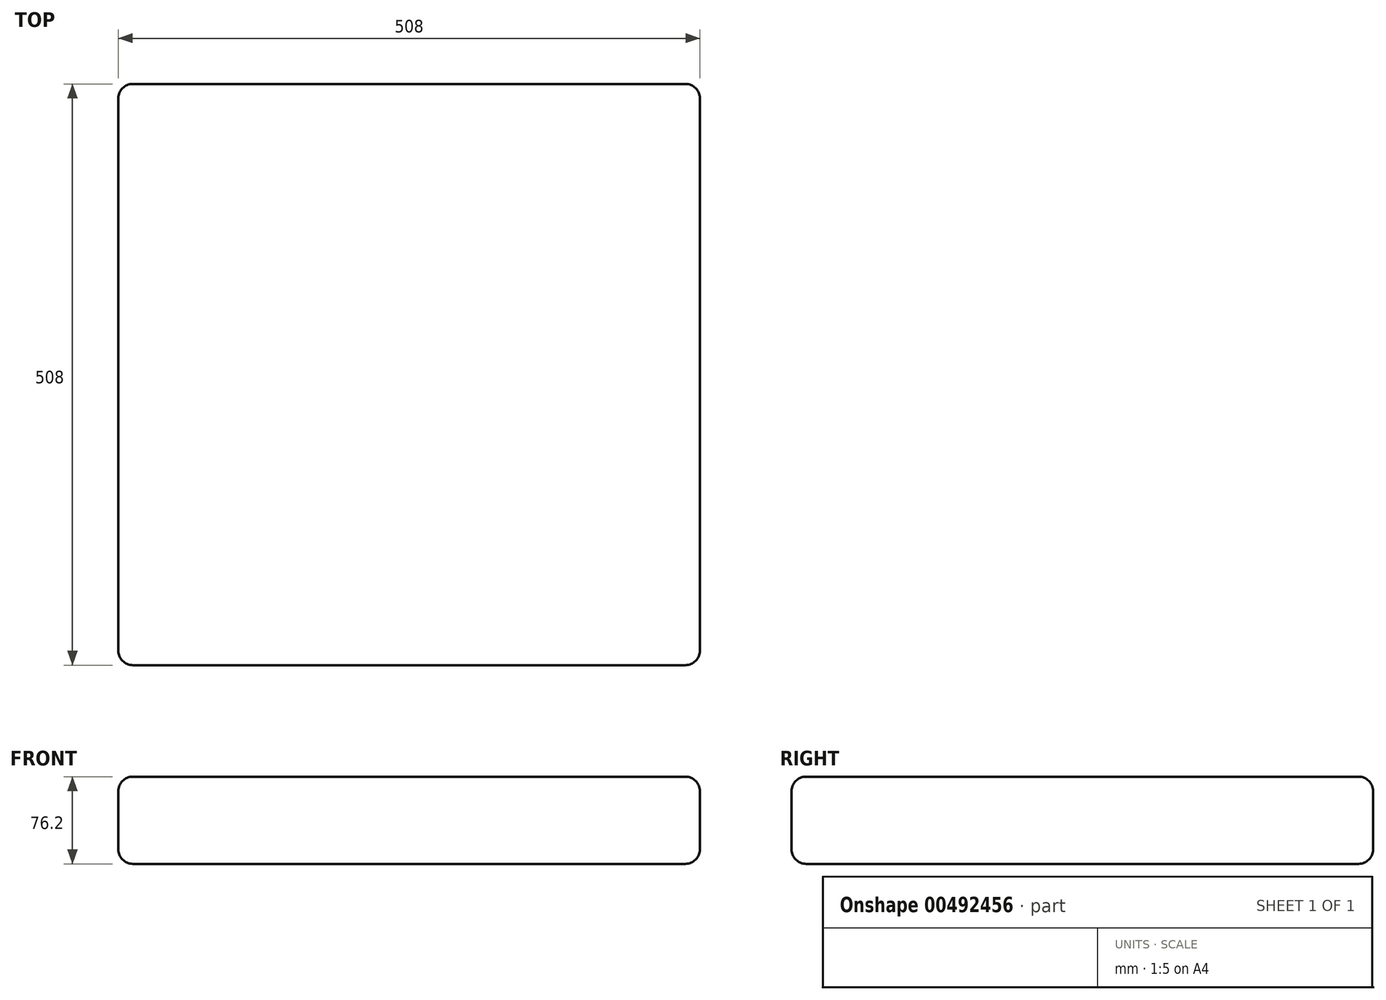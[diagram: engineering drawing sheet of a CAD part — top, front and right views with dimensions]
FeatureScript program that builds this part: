
annotation { "Feature Type Name" : "Feature", "Feature Type Description" : "" }
export const myFeature = defineFeature(function(context is Context, id is Id, definition is map)
    precondition{}
    {
        {
            var Q0;
            Q0=qCreatedBy(makeId("Top.planeOp"),FACE);
            var sketch = newSketch(context, id + "F0", { "sketchPlane" : qUnion([Q0])});
            skLineSegment(sketch, "E0.bottom", {"start": v(254, -254) * mm, "end": v(-254, -254) * mm});
            skLineSegment(sketch, "E0.top", {"start": v(254, 254) * mm, "end": v(-254, 254) * mm});
            skLineSegment(sketch, "E0.left", {"start": v(254, -254) * mm, "end": v(254, 254) * mm});
            skLineSegment(sketch, "E0.right", {"start": v(-254, -254) * mm, "end": v(-254, 254) * mm});
            skPoint(sketch, "E0.middle", {"position": v(0, 0) * mm});
            skSolve(sketch);
        }
        {
            var Q0;
            Q0=makeQuery(id+"F0.imprint","IMPRINT",FACE,{"disambiguationData":[TD([[makeQuery(id+"F0.imprint","IMPRINT",EDGE,{"derivedFrom":sQuery(id+"F0.wireOp",EDGE,"E0.bottom")}),-1.0]])]});
            extrude(context, id + "F1", {"entities" : qUnion([Q0]), "endBound" : BoundingType.SYMMETRIC, "depth" : 76.2 * mm});
        }
        {
            var Q0;
            Q0=makeQuery(id+"F1.opExtrude","CAP_EDGE",EDGE,{"disambiguationData":[OSD([sQuery(id+"F0.wireOp",EDGE,"E0.bottom")])],"isStart":false});
            var Q1;
            Q1=makeQuery(id+"F1.opExtrude","CAP_EDGE",EDGE,{"disambiguationData":[OSD([sQuery(id+"F0.wireOp",EDGE,"E0.right")])],"isStart":false});
            var Q2;
            Q2=makeQuery(id+"F1.opExtrude","CAP_EDGE",EDGE,{"disambiguationData":[OSD([sQuery(id+"F0.wireOp",EDGE,"E0.top")])],"isStart":false});
            var Q3;
            Q3=makeQuery(id+"F1.opExtrude","CAP_EDGE",EDGE,{"disambiguationData":[OSD([sQuery(id+"F0.wireOp",EDGE,"E0.left")])],"isStart":false});
            var Q4;
            Q4=makeQuery(id+"F1.opExtrude","CAP_FACE",FACE,{"disambiguationData":[OSD([sQuery(id+"F0.wireOp",EDGE,"E0.bottom"),sQuery(id+"F0.wireOp",EDGE,"E0.top"),sQuery(id+"F0.wireOp",EDGE,"E0.left"),sQuery(id+"F0.wireOp",EDGE,"E0.right")])],"isStart":false});
            var Q5;
            Q5=makeQuery(id+"F1.opExtrude","SWEPT_FACE",FACE,{"disambiguationData":[OSD([sQuery(id+"F0.wireOp",EDGE,"E0.bottom")])]});
            var Q6;
            Q6=makeQuery(id+"F1.opExtrude","SWEPT_FACE",FACE,{"disambiguationData":[OSD([sQuery(id+"F0.wireOp",EDGE,"E0.left")])]});
            var Q7;
            Q7=makeQuery(id+"F1.opExtrude","SWEPT_FACE",FACE,{"disambiguationData":[OSD([sQuery(id+"F0.wireOp",EDGE,"E0.right")])]});
            var Q8;
            Q8=makeQuery(id+"F1.opExtrude","SWEPT_FACE",FACE,{"disambiguationData":[OSD([sQuery(id+"F0.wireOp",EDGE,"E0.top")])]});
            fillet(context, id + "F2", {"entities" : qUnion([Q0, Q1, Q2, Q3, Q4, Q5, Q6, Q7, Q8]), "radius" : 12.7 * mm, "tangentPropagation" : true, "allowEdgeOverflow" : false});
        }
    });
